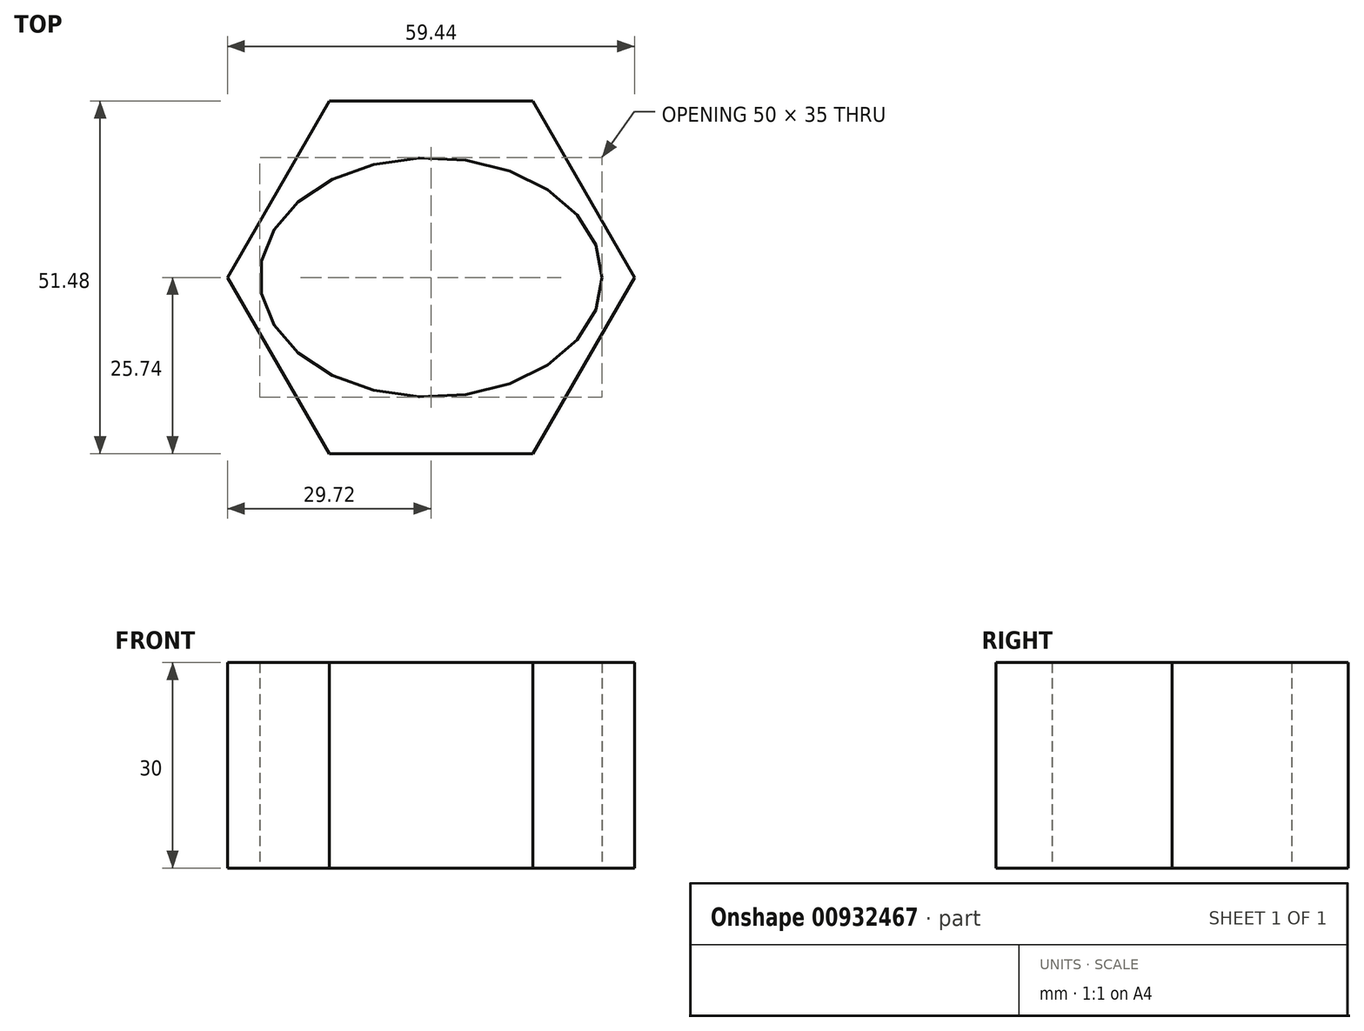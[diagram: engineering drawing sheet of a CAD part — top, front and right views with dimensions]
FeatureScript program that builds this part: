
annotation { "Feature Type Name" : "Feature", "Feature Type Description" : "" }
export const myFeature = defineFeature(function(context is Context, id is Id, definition is map)
    precondition{}
    {
        {
            var Q0;
            Q0=qCreatedBy(makeId("Top.planeOp"),FACE);
            var sketch = newSketch(context, id + "F0", { "sketchPlane" : qUnion([Q0])});
            skEllipse(sketch, "E0", {"center": v(0, 0) * mm, "majorRadius": 25 * mm, "minorRadius": 17.5 * mm, "majorAxis": v(1, 0)});
            skPoint(sketch, "E1.0.midPoint", {"position": v(0, 36.65) * mm});
            skCircle(sketch, "E2.cCircle", {"center": v(0, 0) * mm, "radius": 25.74 * mm, "construction": true});
            skPoint(sketch, "E2.cCircle.perimeterSnap0", {"position": v(0, 17.5) * mm});
            skLineSegment(sketch, "E2.0", {"start": v(-14.86, 25.74) * mm, "end": v(14.86, 25.74) * mm});
            skLineSegment(sketch, "E2.1", {"start": v(14.86, 25.74) * mm, "end": v(29.72, 0) * mm});
            skLineSegment(sketch, "E2.2", {"start": v(29.72, 0) * mm, "end": v(14.86, -25.74) * mm});
            skLineSegment(sketch, "E2.3", {"start": v(14.86, -25.74) * mm, "end": v(-14.86, -25.74) * mm});
            skLineSegment(sketch, "E2.4", {"start": v(-14.86, -25.74) * mm, "end": v(-29.72, 0) * mm});
            skLineSegment(sketch, "E2.5", {"start": v(-29.72, 0) * mm, "end": v(-14.86, 25.74) * mm});
            skPoint(sketch, "E2.0.midPoint", {"position": v(0, 25.74) * mm});
            skPoint(sketch, "E2.0.midPoint.positionSnap0", {"position": v(0, 17.5) * mm});
            skSolve(sketch);
        }
        {
            var Q0;
            Q0 = qSketchRegion(id + "F0", true);
            extrude(context, id + "F1", {"entities" : qUnion([Q0]), "depth" : 30 * mm, "offsetDistance" : 25 * mm});
        }
    });
